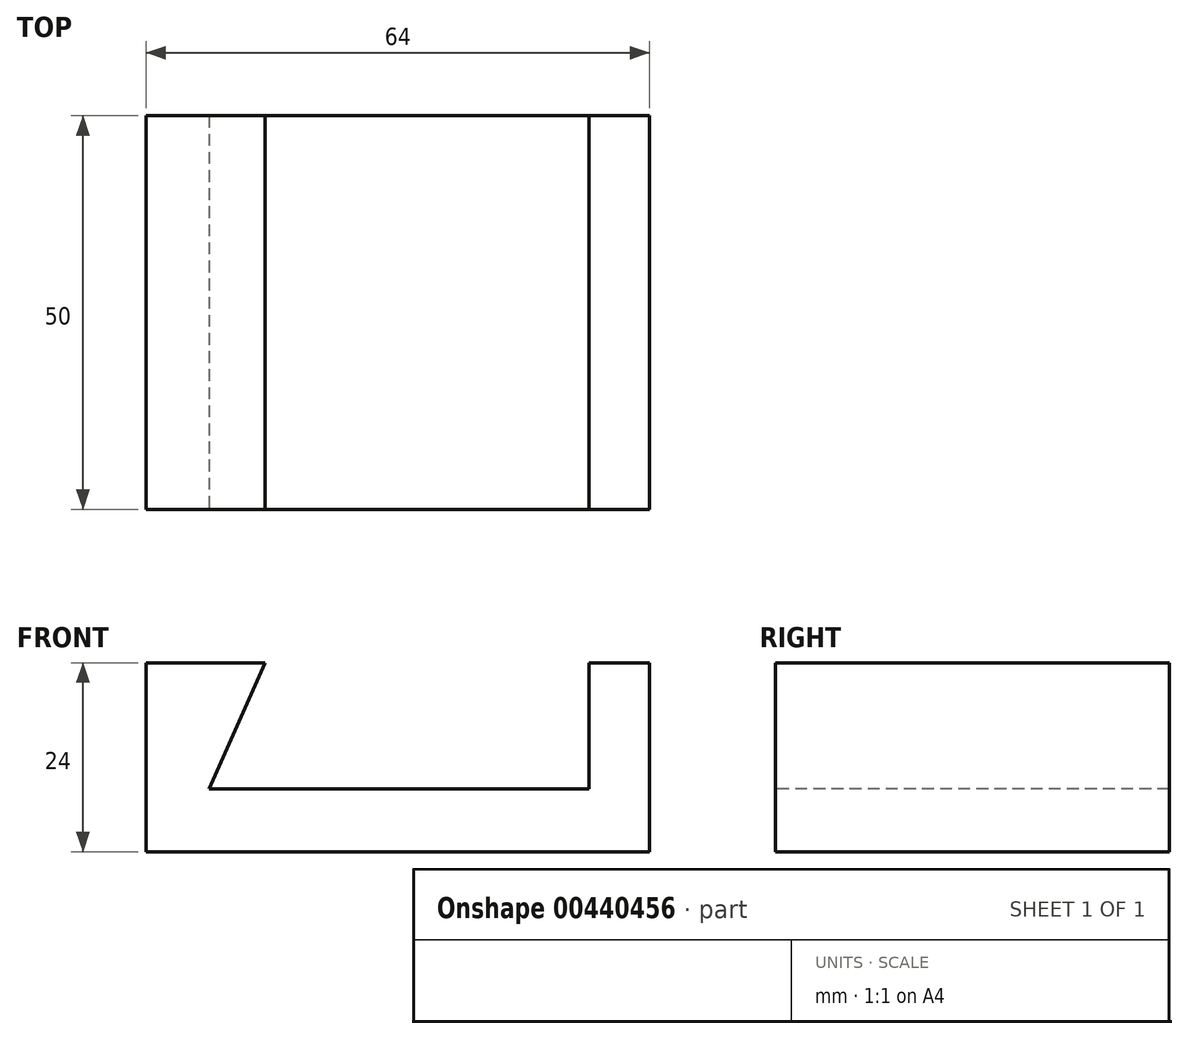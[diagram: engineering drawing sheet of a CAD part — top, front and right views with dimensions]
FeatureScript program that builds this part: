
annotation { "Feature Type Name" : "Feature", "Feature Type Description" : "" }
export const myFeature = defineFeature(function(context is Context, id is Id, definition is map)
    precondition{}
    {
        {
            var Q0;
            Q0=qCreatedBy(makeId("Top.planeOp"),FACE);
            var sketch = newSketch(context, id + "F0", { "sketchPlane" : qUnion([Q0])});
            skLineSegment(sketch, "E0.bottom", {"start": v(-26, 25) * mm, "end": v(38, 25) * mm});
            skLineSegment(sketch, "E0.top", {"start": v(-26, -25) * mm, "end": v(38, -25) * mm});
            skLineSegment(sketch, "E0.left", {"start": v(-26, 25) * mm, "end": v(-26, -25) * mm});
            skLineSegment(sketch, "E0.right", {"start": v(38, 25) * mm, "end": v(38, -25) * mm});
            skSolve(sketch);
        }
        {
            var Q0;
            Q0=makeQuery(id+"F0.imprint","IMPRINT",FACE,{"disambiguationData":[TD([[makeQuery(id+"F0.imprint","IMPRINT",EDGE,{"derivedFrom":sQuery(id+"F0.wireOp",EDGE,"E0.bottom")}),-1.0]])]});
            extrude(context, id + "F1", {"entities" : qUnion([Q0]), "depth" : 24 * mm});
        }
        {
            var Q0;
            Q0=makeQuery(id+"F1.opExtrude","SWEPT_FACE",FACE,{"disambiguationData":[OSD([sQuery(id+"F0.wireOp",EDGE,"E0.top")])]});
            var sketch = newSketch(context, id + "F2", { "sketchPlane" : qUnion([Q0])});
            skLineSegment(sketch, "E1", {"start": v(30.3, 24) * mm, "end": v(30.3, 8) * mm});
            skLineSegment(sketch, "E2", {"start": v(30.3, 8) * mm, "end": v(-18, 8) * mm});
            skLineSegment(sketch, "E3", {"start": v(-18, 8) * mm, "end": v(-10.88, 24) * mm});
            skLineSegment(sketch, "E4", {"start": v(-10.88, 24) * mm, "end": v(30.3, 24) * mm});
            skSolve(sketch);
        }
        {
            var Q0;
            Q0=qSketchRegion(id+"F2",true);
            extrude(context, id + "F3", {"entities" : qUnion([Q0]), "operationType" : NewBodyOperationType.REMOVE, "oppositeDirection" : true, "depth" : 50 * mm});
        }
    });
